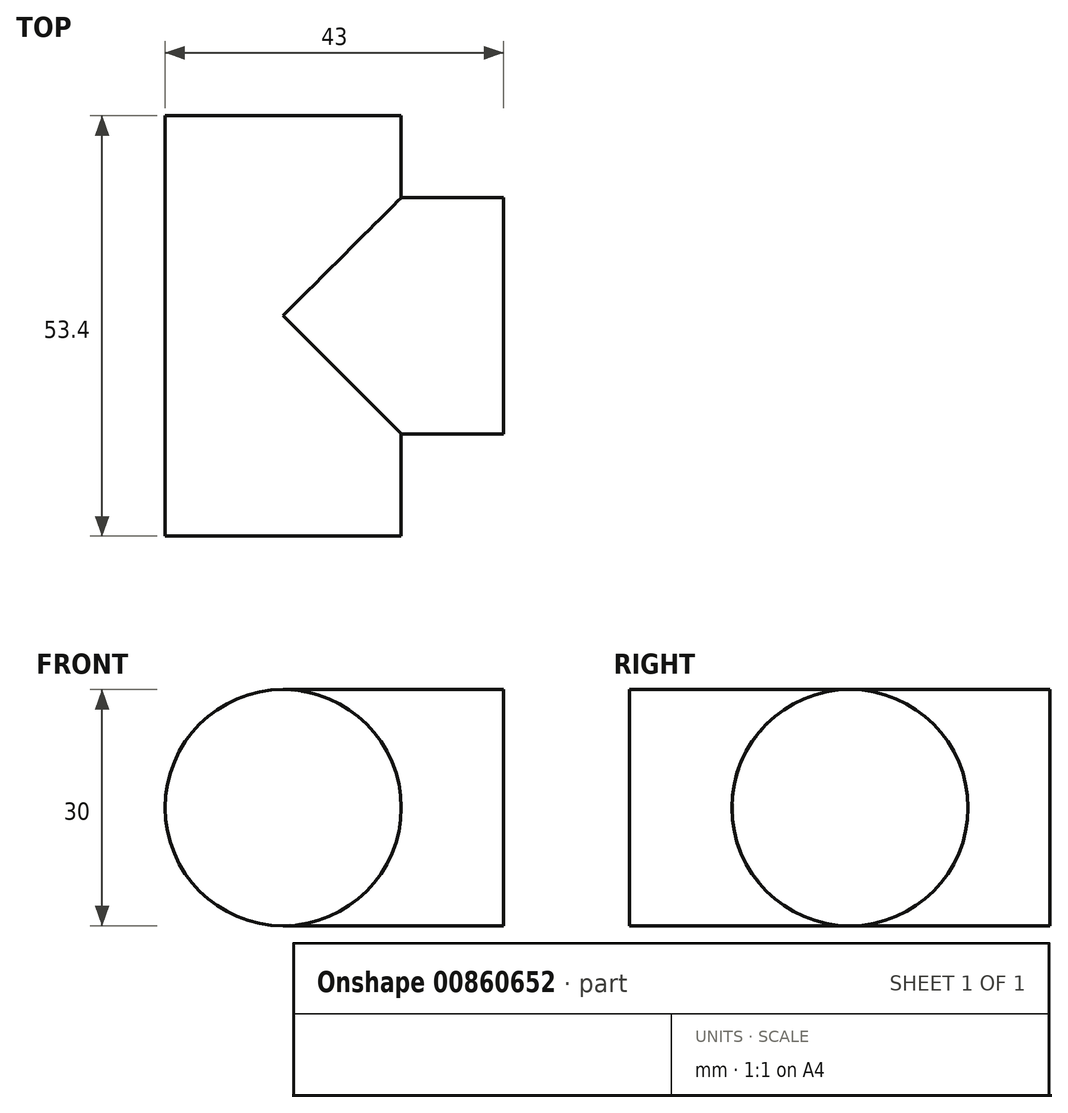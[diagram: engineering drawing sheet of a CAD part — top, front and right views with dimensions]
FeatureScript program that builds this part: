
annotation { "Feature Type Name" : "Feature", "Feature Type Description" : "" }
export const myFeature = defineFeature(function(context is Context, id is Id, definition is map)
    precondition{}
    {
        {
            var Q0;
            Q0=qCreatedBy(makeId("Front.planeOp"),FACE);
            var sketch = newSketch(context, id + "F0", { "sketchPlane" : qUnion([Q0])});
            skCircle(sketch, "E0", {"center": v(0, 0) * mm, "radius": 15 * mm});
            skSolve(sketch);
        }
        {
            var Q0;
            Q0 = qSketchRegion(id + "F0", true);
            extrude(context, id + "F1", {"entities" : qUnion([Q0]), "depth" : 28 * mm, "offsetDistance" : 25.4 * mm});
        }
        {
            var Q0;
            Q0=makeQuery(id+"F1.opExtrude","CAP_FACE",FACE,{"disambiguationData":[OSD([sQuery(id+"F0.wireOp",EDGE,"E0")])],"isStart":true});
            extrude(context, id + "F2", {"entities" : qUnion([Q0]), "operationType" : NewBodyOperationType.ADD, "depth" : 25.4 * mm, "offsetDistance" : 25.4 * mm});
        }
        {
            var Q0;
            Q0=qCreatedBy(makeId("Right.planeOp"),FACE);
            var sketch = newSketch(context, id + "F3", { "sketchPlane" : qUnion([Q0])});
            skCircle(sketch, "E1", {"center": v(0, 0) * mm, "radius": 15 * mm});
            skSolve(sketch);
        }
        {
            var Q0;
            Q0=makeQuery(id+"F3.imprint","IMPRINT",FACE,{"disambiguationData":[TD([[makeQuery(id+"F3.imprint","IMPRINT",EDGE,{"derivedFrom":sQuery(id+"F3.wireOp",EDGE,"E1")}),1.0]])]});
            var Q1;
            Q1=sQuery(id+"F3.wireOp",EDGE,"E1");
            extrude(context, id + "F4", {"entities" : qUnion([Q0]), "operationType" : NewBodyOperationType.ADD, "surfaceEntities" : qUnion([Q1]), "depth" : 28 * mm, "offsetDistance" : 25.4 * mm});
        }
    });
